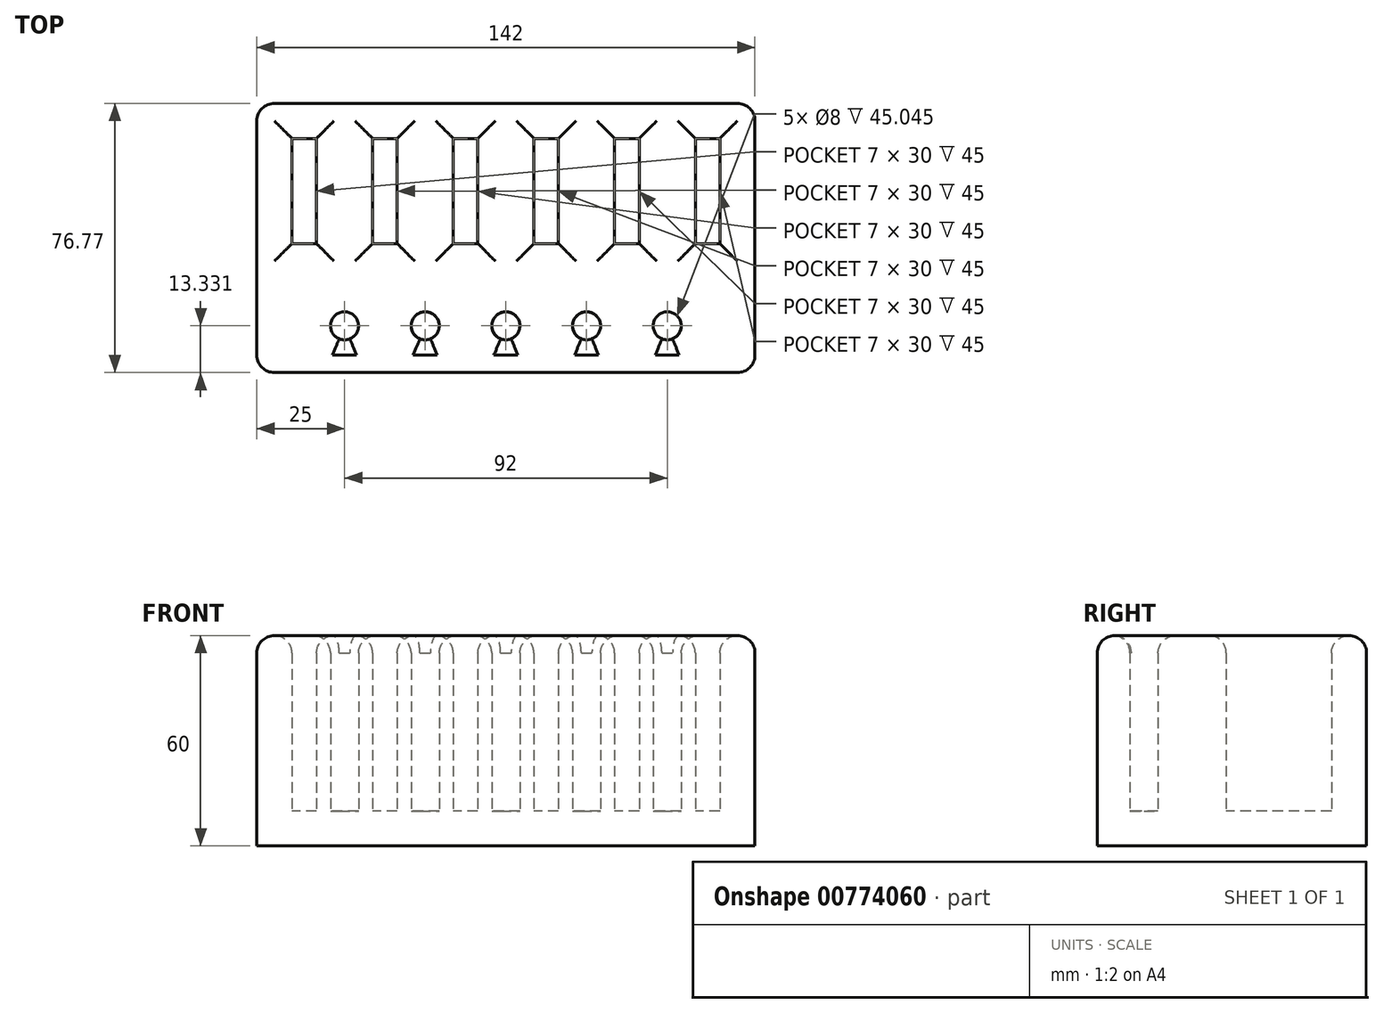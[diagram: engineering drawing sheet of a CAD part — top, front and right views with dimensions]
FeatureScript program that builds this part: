
annotation { "Feature Type Name" : "Feature", "Feature Type Description" : "" }
export const myFeature = defineFeature(function(context is Context, id is Id, definition is map)
    precondition{}
    {
        {
            assignVariable(context, id + "F0", {"name" : "y_margin", "anyValue" : 10 * mm});
        }
        {
            var Q0;
            Q0=qCreatedBy(makeId("Top.planeOp"),FACE);
            var sketch = newSketch(context, id + "F1", { "sketchPlane" : qUnion([Q0])});
            skLineSegment(sketch, "E0.bottom", {"start": v(-7.9, 9.06) * mm, "end": v(134.1, 9.06) * mm});
            skLineSegment(sketch, "E0.top", {"start": v(-7.9, -67.7) * mm, "end": v(134.1, -67.7) * mm});
            skLineSegment(sketch, "E0.left", {"start": v(-7.9, 9.06) * mm, "end": v(-7.9, -67.7) * mm});
            skLineSegment(sketch, "E0.right", {"start": v(134.1, 9.06) * mm, "end": v(134.1, -67.7) * mm});
            skLineSegment(sketch, "E1.bottom", {"start": v(9.1, -0.94) * mm, "end": v(2.1, -0.94) * mm});
            skLineSegment(sketch, "E1.top", {"start": v(9.1, -30.94) * mm, "end": v(2.1, -30.94) * mm});
            skLineSegment(sketch, "E1.left", {"start": v(9.1, -0.94) * mm, "end": v(9.1, -30.94) * mm});
            skLineSegment(sketch, "E1.right", {"start": v(2.1, -0.94) * mm, "end": v(2.1, -30.94) * mm});
            skLineSegment(sketch, "E2.1.0.0", {"start": v(25.1, -0.94) * mm, "end": v(25.1, -30.94) * mm});
            skLineSegment(sketch, "E2.1.0.1", {"start": v(32.1, -0.94) * mm, "end": v(32.1, -30.94) * mm});
            skLineSegment(sketch, "E2.1.0.2", {"start": v(32.1, -30.94) * mm, "end": v(25.1, -30.94) * mm});
            skLineSegment(sketch, "E2.2.0.0", {"start": v(48.1, -0.94) * mm, "end": v(48.1, -30.94) * mm});
            skLineSegment(sketch, "E2.2.0.1", {"start": v(55.1, -0.94) * mm, "end": v(55.1, -30.94) * mm});
            skLineSegment(sketch, "E2.2.0.2", {"start": v(55.1, -30.94) * mm, "end": v(48.1, -30.94) * mm});
            skLineSegment(sketch, "E2.3.0.0", {"start": v(71.1, -0.94) * mm, "end": v(71.1, -30.94) * mm});
            skLineSegment(sketch, "E2.3.0.1", {"start": v(78.1, -0.94) * mm, "end": v(78.1, -30.94) * mm});
            skLineSegment(sketch, "E2.3.0.2", {"start": v(78.1, -30.94) * mm, "end": v(71.1, -30.94) * mm});
            skLineSegment(sketch, "E2.4.0.0", {"start": v(94.1, -0.94) * mm, "end": v(94.1, -30.94) * mm});
            skLineSegment(sketch, "E2.4.0.1", {"start": v(101.1, -0.94) * mm, "end": v(101.1, -30.94) * mm});
            skLineSegment(sketch, "E2.4.0.2", {"start": v(101.1, -30.94) * mm, "end": v(94.1, -30.94) * mm});
            skLineSegment(sketch, "E2.direction1", {"start": v(2.1, -30.94) * mm, "end": v(25.1, -30.94) * mm, "construction": true});
            skLineSegment(sketch, "E3.0.5.0", {"start": v(117.1, -0.94) * mm, "end": v(117.1, -30.94) * mm});
            skLineSegment(sketch, "E3.3.5.0", {"start": v(124.1, -0.94) * mm, "end": v(124.1, -30.94) * mm});
            skLineSegment(sketch, "E3.6.5.0", {"start": v(124.1, -30.94) * mm, "end": v(117.1, -30.94) * mm});
            skLineSegment(sketch, "E4", {"start": v(25.1, -0.94) * mm, "end": v(32.1, -0.94) * mm});
            skLineSegment(sketch, "E5", {"start": v(48.1, -0.94) * mm, "end": v(55.1, -0.94) * mm});
            skLineSegment(sketch, "E6", {"start": v(71.1, -0.94) * mm, "end": v(78.1, -0.94) * mm});
            skLineSegment(sketch, "E7", {"start": v(94.1, -0.94) * mm, "end": v(101.1, -0.94) * mm});
            skLineSegment(sketch, "E8", {"start": v(117.1, -0.94) * mm, "end": v(124.1, -0.94) * mm});
            skLineSegment(sketch, "E9", {"start": v(-7.9, -0.94) * mm, "end": v(134.1, -0.94) * mm, "construction": true});
            skCircle(sketch, "E10", {"center": v(17.1, -54.38) * mm, "radius": 4 * mm});
            skCircle(sketch, "E11.1.0.0", {"center": v(40.1, -54.38) * mm, "radius": 4 * mm});
            skCircle(sketch, "E11.2.0.0", {"center": v(63.1, -54.38) * mm, "radius": 4 * mm});
            skCircle(sketch, "E11.3.0.0", {"center": v(86.1, -54.38) * mm, "radius": 4 * mm});
            skCircle(sketch, "E11.4.0.0", {"center": v(109.1, -54.38) * mm, "radius": 4 * mm});
            skLineSegment(sketch, "E11.direction1", {"start": v(17.1, -54.38) * mm, "end": v(40.1, -54.38) * mm, "construction": true});
            skSolve(sketch);
        }
        {
            var Q0;
            Q0=makeQuery(id+"F1.imprint","IMPRINT",FACE,{"disambiguationData":[TD([[makeQuery(id+"F1.imprint","IMPRINT",EDGE,{"derivedFrom":sQuery(id+"F1.wireOp",EDGE,"E0.bottom")}),-1.0]])]});
            extrude(context, id + "F2", {"entities" : qUnion([Q0]), "depth" : 50 * mm, "offsetDistance" : 25 * mm});
        }
        {
            var Q0;
            Q0=makeQuery(id+"F2.opExtrude","CAP_FACE",FACE,{"disambiguationData":[OSD([sQuery(id+"F1.wireOp",EDGE,"E0.bottom"),sQuery(id+"F1.wireOp",EDGE,"E0.top"),sQuery(id+"F1.wireOp",EDGE,"E0.left"),sQuery(id+"F1.wireOp",EDGE,"E0.right"),sQuery(id+"F1.wireOp",EDGE,"E1.bottom"),sQuery(id+"F1.wireOp",EDGE,"E1.top"),sQuery(id+"F1.wireOp",EDGE,"E1.left"),sQuery(id+"F1.wireOp",EDGE,"E1.right"),sQuery(id+"F1.wireOp",EDGE,"E2.1.0.0"),sQuery(id+"F1.wireOp",EDGE,"E2.1.0.1"),sQuery(id+"F1.wireOp",EDGE,"E2.1.0.2"),sQuery(id+"F1.wireOp",EDGE,"E2.2.0.0"),sQuery(id+"F1.wireOp",EDGE,"E2.2.0.1"),sQuery(id+"F1.wireOp",EDGE,"E2.2.0.2"),sQuery(id+"F1.wireOp",EDGE,"E2.3.0.0"),sQuery(id+"F1.wireOp",EDGE,"E2.3.0.1"),sQuery(id+"F1.wireOp",EDGE,"E2.3.0.2"),sQuery(id+"F1.wireOp",EDGE,"E2.4.0.0"),sQuery(id+"F1.wireOp",EDGE,"E2.4.0.1"),sQuery(id+"F1.wireOp",EDGE,"E2.4.0.2"),sQuery(id+"F1.wireOp",EDGE,"E3.0.5.0"),sQuery(id+"F1.wireOp",EDGE,"E3.3.5.0"),sQuery(id+"F1.wireOp",EDGE,"E3.6.5.0"),sQuery(id+"F1.wireOp",EDGE,"E4"),sQuery(id+"F1.wireOp",EDGE,"E5"),sQuery(id+"F1.wireOp",EDGE,"E6"),sQuery(id+"F1.wireOp",EDGE,"E7"),sQuery(id+"F1.wireOp",EDGE,"E8"),sQuery(id+"F1.wireOp",EDGE,"E10"),sQuery(id+"F1.wireOp",EDGE,"E11.1.0.0"),sQuery(id+"F1.wireOp",EDGE,"E11.2.0.0"),sQuery(id+"F1.wireOp",EDGE,"E11.3.0.0"),sQuery(id+"F1.wireOp",EDGE,"E11.4.0.0")])],"isStart":true});
            var sketch = newSketch(context, id + "F3", { "sketchPlane" : qUnion([Q0])});
            skLineSegment(sketch, "E12.bottom", {"start": v(-7.9, -9.06) * mm, "end": v(134.1, -9.06) * mm});
            skLineSegment(sketch, "E12.top", {"start": v(-7.9, 67.7) * mm, "end": v(134.1, 67.7) * mm});
            skLineSegment(sketch, "E12.left", {"start": v(-7.9, -9.06) * mm, "end": v(-7.9, 67.7) * mm});
            skLineSegment(sketch, "E12.right", {"start": v(134.1, -9.06) * mm, "end": v(134.1, 67.7) * mm});
            skSolve(sketch);
        }
        {
            var Q0;
            Q0 = qSketchRegion(id + "F3", true);
            extrude(context, id + "F4", {"entities" : qUnion([Q0]), "operationType" : NewBodyOperationType.ADD, "depth" : getVariable(context, 'y_margin'), "offsetDistance" : 25 * mm});
        }
        {
            var Q0;
            Q0=makeQuery(id+"F4.boolean.opBoolean","MERGE",EDGE,{"derivedFrom":[makeQuery(id+"F2.opExtrude","SWEPT_EDGE",EDGE,{"disambiguationData":[OSD([sQuery(id+"F1.wireOp",EDGE,"E0.bottom"),sQuery(id+"F1.wireOp",EDGE,"E0.left")])]}),makeQuery(id+"F4.opExtrude","SWEPT_EDGE",EDGE,{"disambiguationData":[OSD([sQuery(id+"F3.wireOp",EDGE,"E12.bottom"),sQuery(id+"F3.wireOp",EDGE,"E12.left")])]})]});
            var Q1;
            Q1=makeQuery(id+"F4.boolean.opBoolean","MERGE",EDGE,{"derivedFrom":[makeQuery(id+"F2.opExtrude","SWEPT_EDGE",EDGE,{"disambiguationData":[OSD([sQuery(id+"F1.wireOp",EDGE,"E0.top"),sQuery(id+"F1.wireOp",EDGE,"E0.left")])]}),makeQuery(id+"F4.opExtrude","SWEPT_EDGE",EDGE,{"disambiguationData":[OSD([sQuery(id+"F3.wireOp",EDGE,"E12.top"),sQuery(id+"F3.wireOp",EDGE,"E12.left")])]})]});
            var Q2;
            Q2=makeQuery(id+"F4.boolean.opBoolean","MERGE",EDGE,{"derivedFrom":[makeQuery(id+"F2.opExtrude","SWEPT_EDGE",EDGE,{"disambiguationData":[OSD([sQuery(id+"F1.wireOp",EDGE,"E0.bottom"),sQuery(id+"F1.wireOp",EDGE,"E0.right")])]}),makeQuery(id+"F4.opExtrude","SWEPT_EDGE",EDGE,{"disambiguationData":[OSD([sQuery(id+"F3.wireOp",EDGE,"E12.bottom"),sQuery(id+"F3.wireOp",EDGE,"E12.right")])]})]});
            var Q3;
            Q3=makeQuery(id+"F4.boolean.opBoolean","MERGE",EDGE,{"derivedFrom":[makeQuery(id+"F2.opExtrude","SWEPT_EDGE",EDGE,{"disambiguationData":[OSD([sQuery(id+"F1.wireOp",EDGE,"E0.top"),sQuery(id+"F1.wireOp",EDGE,"E0.right")])]}),makeQuery(id+"F4.opExtrude","SWEPT_EDGE",EDGE,{"disambiguationData":[OSD([sQuery(id+"F3.wireOp",EDGE,"E12.top"),sQuery(id+"F3.wireOp",EDGE,"E12.right")])]})]});
            var Q4;
            Q4=makeQuery(id+"F2.opExtrude","CAP_EDGE",EDGE,{"disambiguationData":[OSD([sQuery(id+"F1.wireOp",EDGE,"E0.bottom")])],"isStart":false});
            var Q5;
            Q5=makeQuery(id+"F2.opExtrude","CAP_EDGE",EDGE,{"disambiguationData":[OSD([sQuery(id+"F1.wireOp",EDGE,"E0.left")])],"isStart":false});
            var Q6;
            Q6=makeQuery(id+"F2.opExtrude","CAP_EDGE",EDGE,{"disambiguationData":[OSD([sQuery(id+"F1.wireOp",EDGE,"E0.top")])],"isStart":false});
            var Q7;
            Q7=makeQuery(id+"F2.opExtrude","CAP_EDGE",EDGE,{"disambiguationData":[OSD([sQuery(id+"F1.wireOp",EDGE,"E0.right")])],"isStart":false});
            fillet(context, id + "F5", {"entities" : qUnion([Q0, Q1, Q2, Q3, Q4, Q5, Q6, Q7]), "radius" : 5 * mm, "tangentPropagation" : true, "allowEdgeOverflow" : false});
        }
        {
            var Q0;
            Q0=makeQuery(id+"F2.opExtrude","CAP_FACE",FACE,{"disambiguationData":[OSD([sQuery(id+"F1.wireOp",EDGE,"E0.bottom"),sQuery(id+"F1.wireOp",EDGE,"E0.top"),sQuery(id+"F1.wireOp",EDGE,"E0.left"),sQuery(id+"F1.wireOp",EDGE,"E0.right"),sQuery(id+"F1.wireOp",EDGE,"E1.bottom"),sQuery(id+"F1.wireOp",EDGE,"E1.top"),sQuery(id+"F1.wireOp",EDGE,"E1.left"),sQuery(id+"F1.wireOp",EDGE,"E1.right"),sQuery(id+"F1.wireOp",EDGE,"E2.1.0.0"),sQuery(id+"F1.wireOp",EDGE,"E2.1.0.1"),sQuery(id+"F1.wireOp",EDGE,"E2.1.0.2"),sQuery(id+"F1.wireOp",EDGE,"E2.2.0.0"),sQuery(id+"F1.wireOp",EDGE,"E2.2.0.1"),sQuery(id+"F1.wireOp",EDGE,"E2.2.0.2"),sQuery(id+"F1.wireOp",EDGE,"E2.3.0.0"),sQuery(id+"F1.wireOp",EDGE,"E2.3.0.1"),sQuery(id+"F1.wireOp",EDGE,"E2.3.0.2"),sQuery(id+"F1.wireOp",EDGE,"E2.4.0.0"),sQuery(id+"F1.wireOp",EDGE,"E2.4.0.1"),sQuery(id+"F1.wireOp",EDGE,"E2.4.0.2"),sQuery(id+"F1.wireOp",EDGE,"E3.0.5.0"),sQuery(id+"F1.wireOp",EDGE,"E3.3.5.0"),sQuery(id+"F1.wireOp",EDGE,"E3.6.5.0"),sQuery(id+"F1.wireOp",EDGE,"E4"),sQuery(id+"F1.wireOp",EDGE,"E5"),sQuery(id+"F1.wireOp",EDGE,"E6"),sQuery(id+"F1.wireOp",EDGE,"E7"),sQuery(id+"F1.wireOp",EDGE,"E8"),sQuery(id+"F1.wireOp",EDGE,"E10"),sQuery(id+"F1.wireOp",EDGE,"E11.1.0.0"),sQuery(id+"F1.wireOp",EDGE,"E11.2.0.0"),sQuery(id+"F1.wireOp",EDGE,"E11.3.0.0"),sQuery(id+"F1.wireOp",EDGE,"E11.4.0.0")])],"isStart":false});
            fillet(context, id + "F6", {"entities" : qUnion([Q0]), "radius" : 5 * mm, "tangentPropagation" : true, "allowEdgeOverflow" : false});
        }
    });
